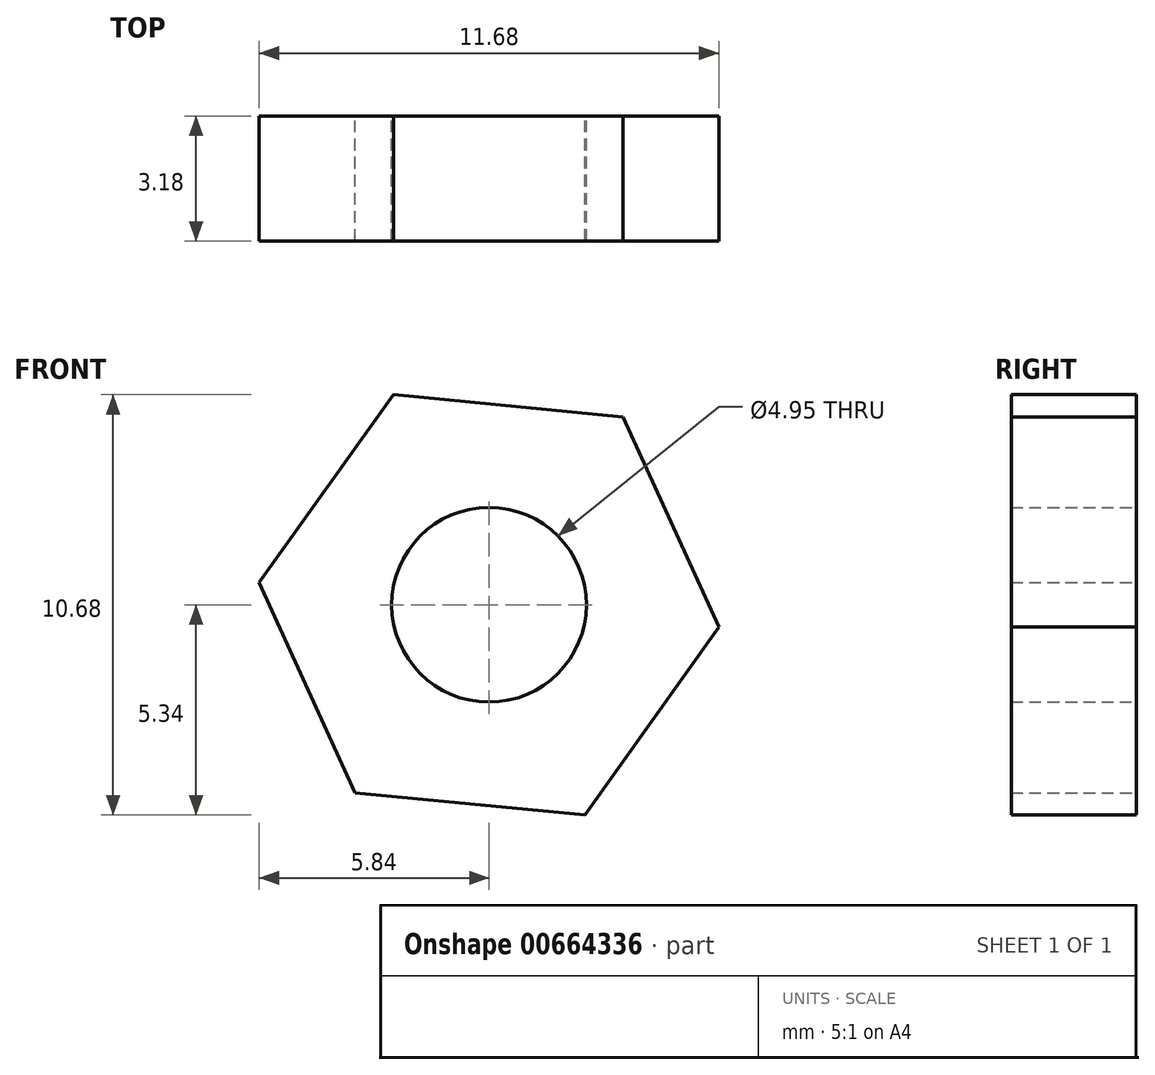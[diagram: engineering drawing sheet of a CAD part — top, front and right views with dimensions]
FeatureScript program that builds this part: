
annotation { "Feature Type Name" : "Feature", "Feature Type Description" : "" }
export const myFeature = defineFeature(function(context is Context, id is Id, definition is map)
    precondition{}
    {
        {
            var Q0;
            Q0=qCreatedBy(makeId("Front.planeOp"),FACE);
            var sketch = newSketch(context, id + "F0", { "sketchPlane" : qUnion([Q0])});
            skCircle(sketch, "E0", {"center": v(0, 0) * mm, "radius": 2.47 * mm});
            skCircle(sketch, "E1.cCircle", {"center": v(0, 0) * mm, "radius": 5.08 * mm, "construction": true});
            skLineSegment(sketch, "E1.0", {"start": v(3.4, 4.77) * mm, "end": v(5.84, -0.56) * mm});
            skLineSegment(sketch, "E1.1", {"start": v(5.84, -0.56) * mm, "end": v(2.43, -5.34) * mm});
            skLineSegment(sketch, "E1.2", {"start": v(2.43, -5.34) * mm, "end": v(-3.4, -4.77) * mm});
            skLineSegment(sketch, "E1.3", {"start": v(-3.4, -4.77) * mm, "end": v(-5.84, 0.56) * mm});
            skLineSegment(sketch, "E1.4", {"start": v(-5.84, 0.56) * mm, "end": v(-2.43, 5.34) * mm});
            skLineSegment(sketch, "E1.5", {"start": v(-2.43, 5.34) * mm, "end": v(3.4, 4.77) * mm});
            skPoint(sketch, "E1.0.midPoint", {"position": v(4.62, 2.1) * mm});
            skSolve(sketch);
        }
        {
            var Q0;
            Q0=qSketchRegion(id+"F0",true);
            extrude(context, id + "F1", {"entities" : qUnion([Q0]), "depth" : 3.17 * mm, "offsetDistance" : 25.4 * mm});
        }
    });
